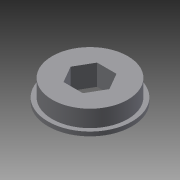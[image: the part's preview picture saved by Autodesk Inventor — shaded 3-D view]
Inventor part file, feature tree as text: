
AUTODESK INVENTOR PART (.ipt)
format: ipt  version: 2013 (Build 170138000, 138)  size: 96,768 bytes
history: native  units: in
note: dims shown in document units (in); Inventor stores cm internally (conversion verified against a paired STEP export)
features: extrude x2, sketch x2
ambient origin geometry x8: Origin, YZ Plane, XZ Plane, XY Plane, X Axis, Y Axis, Z Axis, Center Point
bodies: Solid1 (feature_tree)
feature tree (4):
  extrude  "Extrusion1"  Depth=1.25in
  extrude  "Extrusion2"  Depth=1.125in
  sketch  "Sketch1"  dims[d0=0.5in d1=1.25in]
  sketch  "Sketch2"  dims[d2=0.062in d3=0.0in d4=1.125in d5=0.25in d6=0.0in]
